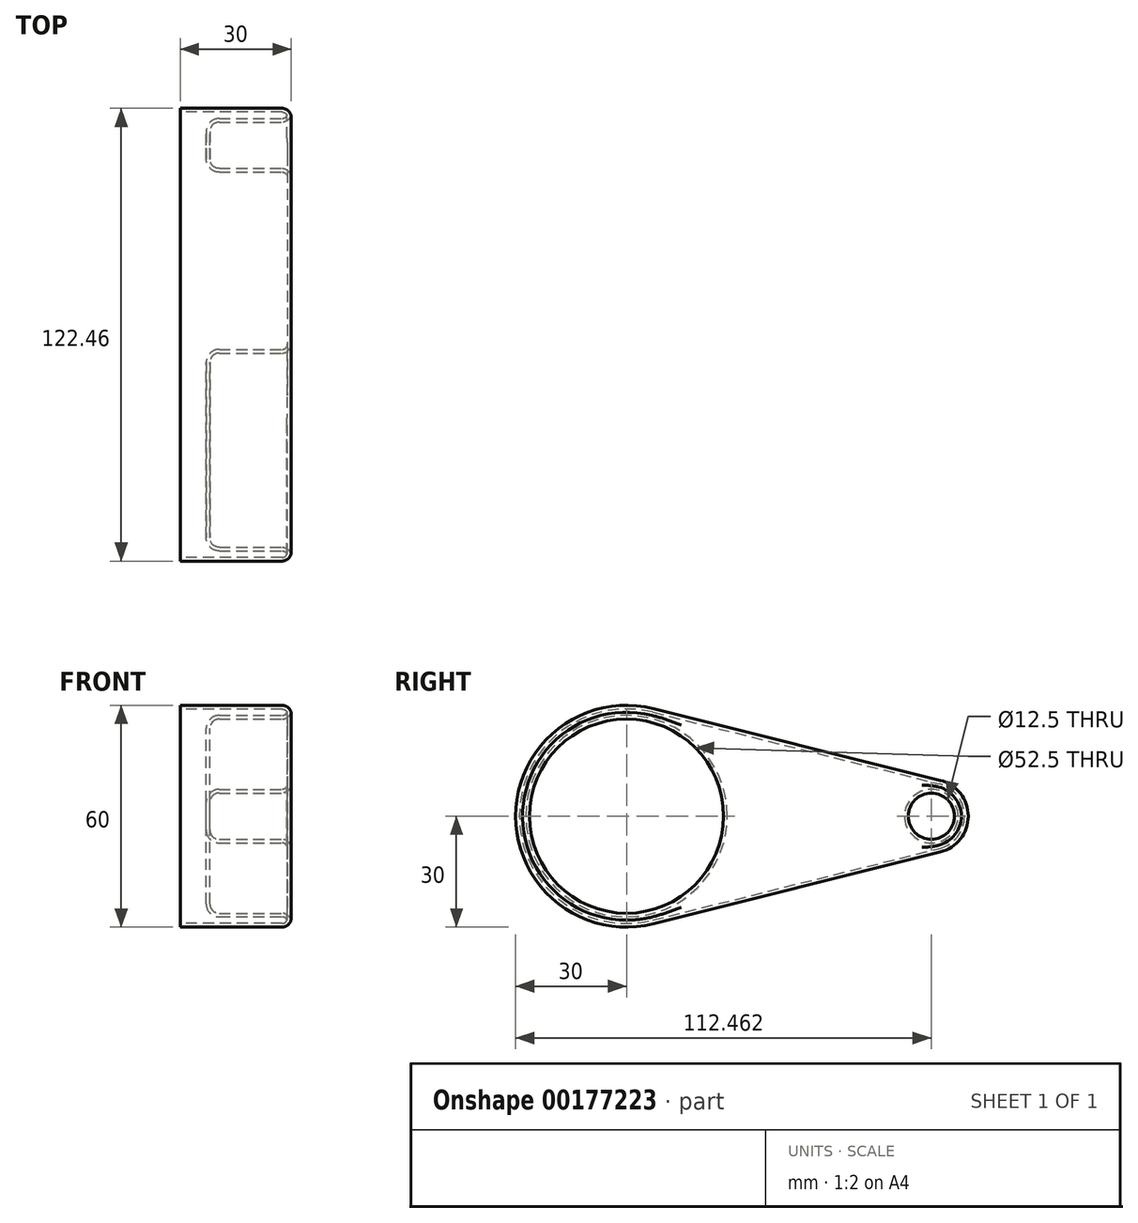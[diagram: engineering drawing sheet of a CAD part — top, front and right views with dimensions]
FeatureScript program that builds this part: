
annotation { "Feature Type Name" : "Feature", "Feature Type Description" : "" }
export const myFeature = defineFeature(function(context is Context, id is Id, definition is map)
    precondition{}
    {
        {
            var Q0;
            Q0=qCreatedBy(makeId("Right.planeOp"),FACE);
            var sketch = newSketch(context, id + "F0", { "sketchPlane" : qUnion([Q0])});
            skCircle(sketch, "E0", {"center": v(0, 0) * mm, "radius": 30 * mm});
            skCircle(sketch, "E1", {"center": v(82.46, 0) * mm, "radius": 10 * mm});
            skLineSegment(sketch, "E2", {"start": v(7.28, 29.1) * mm, "end": v(84.89, 9.7) * mm});
            skLineSegment(sketch, "E3", {"start": v(7.28, -29.1) * mm, "end": v(84.89, -9.7) * mm});
            skSolve(sketch);
        }
        {
            var Q0;
            Q0 = qSketchRegion(id + "F0", true);
            extrude(context, id + "F1", {"entities" : qUnion([Q0]), "depth" : 30 * mm});
        }
        {
            var Q0;
            Q0=makeQuery(id+"F1.opExtrude","CAP_FACE",FACE,{"disambiguationData":[OSD([sQuery(id+"F0.wireOp",EDGE,"E0"),sQuery(id+"F0.wireOp",EDGE,"E1"),sQuery(id+"F0.wireOp",EDGE,"E2"),sQuery(id+"F0.wireOp",EDGE,"E3")])],"isStart":false});
            var sketch = newSketch(context, id + "F2", { "sketchPlane" : qUnion([Q0])});
            skCircle(sketch, "E4", {"center": v(0, 0) * mm, "radius": 26.25 * mm});
            skCircle(sketch, "E5", {"center": v(82.46, 0) * mm, "radius": 6.25 * mm});
            skSolve(sketch);
        }
        {
            var Q0;
            Q0 = qSketchRegion(id + "F2", true);
            extrude(context, id + "F3", {"entities" : qUnion([Q0]), "operationType" : NewBodyOperationType.REMOVE, "oppositeDirection" : true, "depth" : 22 * mm});
        }
        {
            var Q0;
            Q0=makeQuery(id+"F1.opExtrude","CAP_FACE",FACE,{"disambiguationData":[OSD([sQuery(id+"F0.wireOp",EDGE,"E0"),sQuery(id+"F0.wireOp",EDGE,"E1"),sQuery(id+"F0.wireOp",EDGE,"E2"),sQuery(id+"F0.wireOp",EDGE,"E3")])],"isStart":false});
            var Q1;
            Q1=makeQuery(id+"F3.boolean.opBoolean","COPY",FACE,{"derivedFrom":makeQuery(id+"F3.opExtrude","CAP_FACE",FACE,{"disambiguationData":[OSD([sQuery(id+"F2.wireOp",EDGE,"E4")])],"isStart":false})});
            var Q2;
            Q2=makeQuery(id+"F3.boolean.opBoolean","COPY",FACE,{"derivedFrom":makeQuery(id+"F3.opExtrude","CAP_FACE",FACE,{"disambiguationData":[OSD([sQuery(id+"F2.wireOp",EDGE,"E5")])],"isStart":false})});
            fillet(context, id + "F4", {"entities" : qUnion([Q0, Q1, Q2]), "radius" : 2.5 * mm, "tangentPropagation" : true, "allowEdgeOverflow" : false});
        }
        {
            var Q0;
            Q0=makeQuery(id+"F1.opExtrude","CAP_FACE",FACE,{"disambiguationData":[OSD([sQuery(id+"F0.wireOp",EDGE,"E0"),sQuery(id+"F0.wireOp",EDGE,"E1"),sQuery(id+"F0.wireOp",EDGE,"E2"),sQuery(id+"F0.wireOp",EDGE,"E3")])],"isStart":true});
            shell(context, id + "F5", {"entities" : qUnion([Q0]), "thickness" : 1 * mm});
        }
    });
